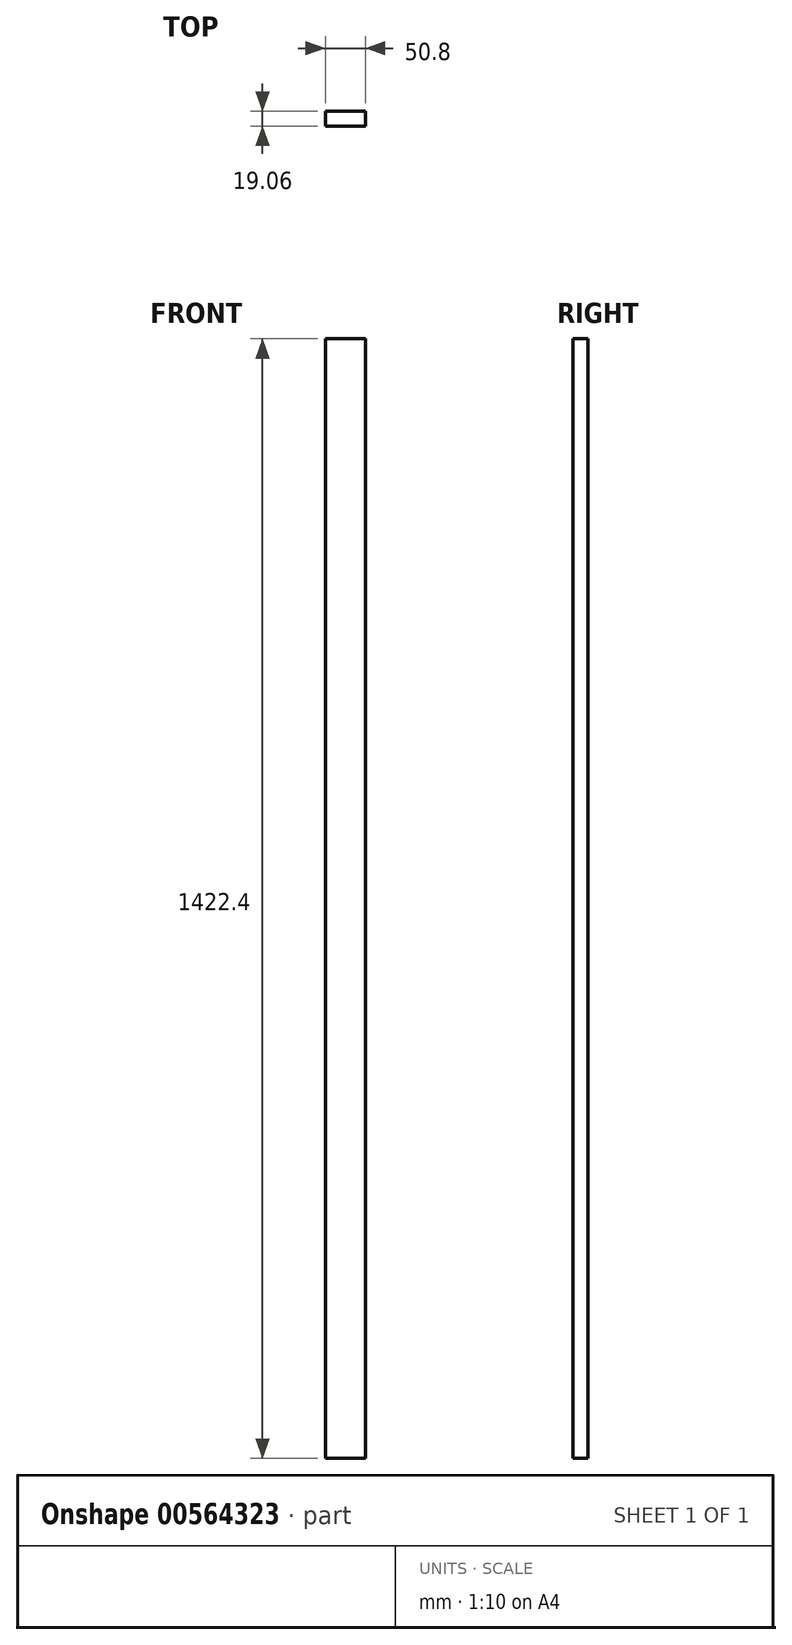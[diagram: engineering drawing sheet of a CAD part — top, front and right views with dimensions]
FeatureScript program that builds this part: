
annotation { "Feature Type Name" : "Feature", "Feature Type Description" : "" }
export const myFeature = defineFeature(function(context is Context, id is Id, definition is map)
    precondition{}
    {
        {
            var Q0;
            Q0=qCreatedBy(makeId("Top.planeOp"),FACE);
            var sketch = newSketch(context, id + "F0", { "sketchPlane" : qUnion([Q0])});
            skLineSegment(sketch, "E0.bottom", {"start": v(-25.4, 9.53) * mm, "end": v(25.4, 9.53) * mm});
            skLineSegment(sketch, "E0.top", {"start": v(-25.4, -9.53) * mm, "end": v(25.4, -9.53) * mm});
            skLineSegment(sketch, "E0.left", {"start": v(-25.4, 9.53) * mm, "end": v(-25.4, -9.53) * mm});
            skLineSegment(sketch, "E0.right", {"start": v(25.4, 9.53) * mm, "end": v(25.4, -9.53) * mm});
            skPoint(sketch, "E0.middle", {"position": v(0, 0) * mm});
            skSolve(sketch);
        }
        {
            var Q0;
            Q0 = qSketchRegion(id + "F0", true);
            extrude(context, id + "F1", {"entities" : qUnion([Q0]), "endBound" : BoundingType.SYMMETRIC, "depth" : 1422.4 * mm, "offsetDistance" : 25.4 * mm});
        }
    });
